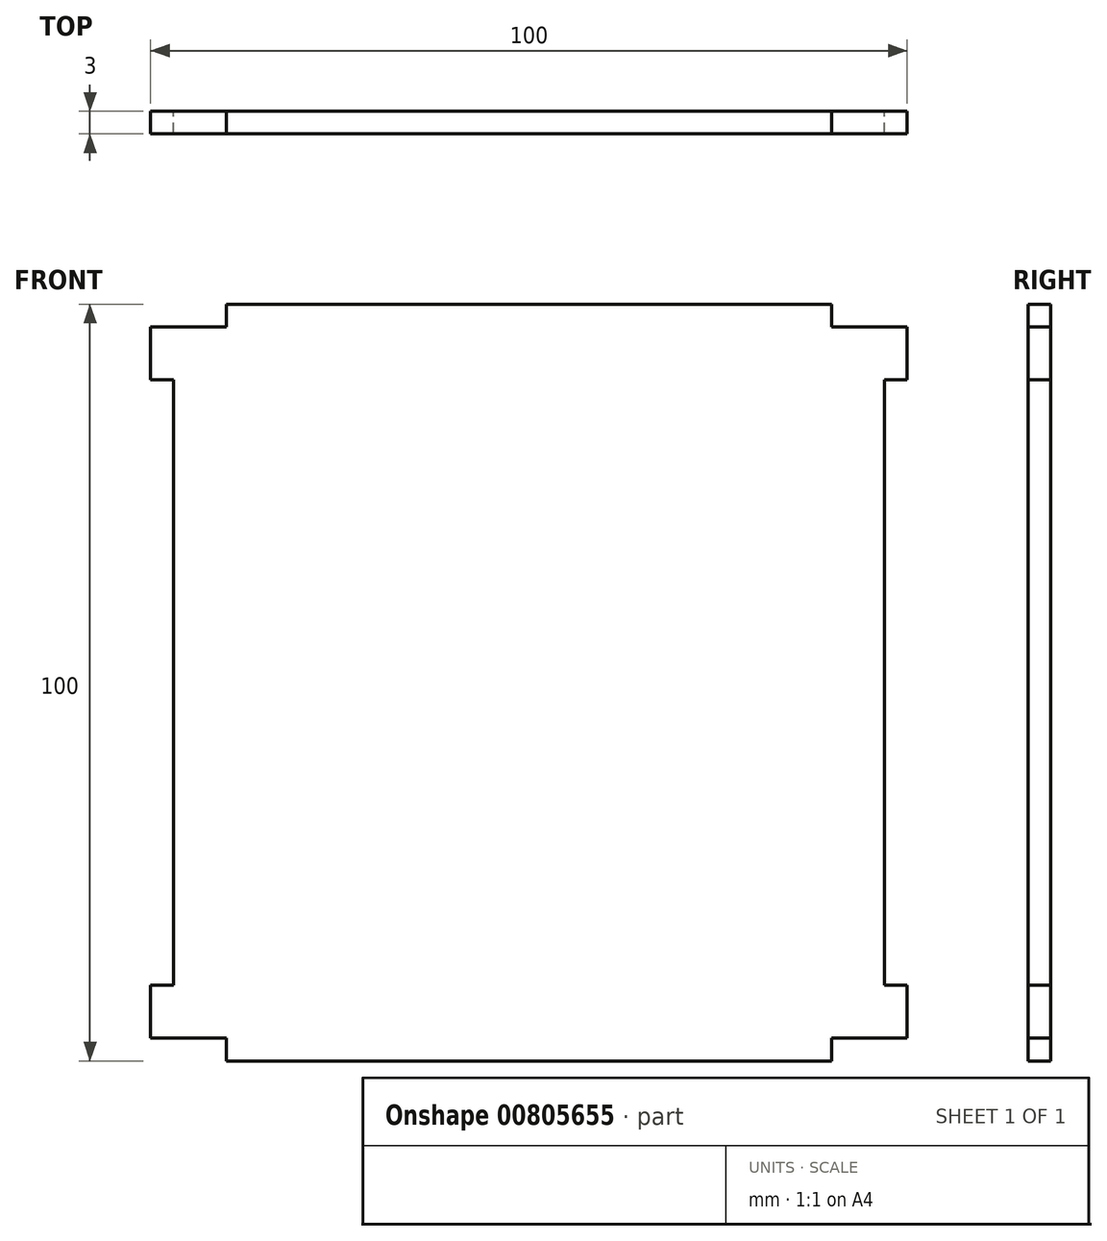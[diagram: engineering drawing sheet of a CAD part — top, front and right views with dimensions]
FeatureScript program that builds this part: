
annotation { "Feature Type Name" : "Feature", "Feature Type Description" : "" }
export const myFeature = defineFeature(function(context is Context, id is Id, definition is map)
    precondition{}
    {
        {
            var Q0;
            Q0=qCreatedBy(makeId("Front.planeOp"),FACE);
            var sketch = newSketch(context, id + "F0", { "sketchPlane" : qUnion([Q0])});
            skLineSegment(sketch, "E0.bottom", {"start": v(10, 0) * mm, "end": v(90, 0) * mm});
            skLineSegment(sketch, "E0.top", {"start": v(10, 100) * mm, "end": v(90, 100) * mm});
            skLineSegment(sketch, "E0.left", {"start": v(0, 3) * mm, "end": v(0, 10) * mm});
            skLineSegment(sketch, "E0.right", {"start": v(100, 3) * mm, "end": v(100, 10) * mm});
            skLineSegment(sketch, "E1", {"start": v(10, 100) * mm, "end": v(10, 97) * mm});
            skLineSegment(sketch, "E2", {"start": v(10, 97) * mm, "end": v(0, 97) * mm});
            skLineSegment(sketch, "E3", {"start": v(50, 100) * mm, "end": v(50, 0) * mm, "construction": true});
            skLineSegment(sketch, "E4", {"start": v(3, 50) * mm, "end": v(97, 50) * mm, "construction": true});
            skPoint(sketch, "E5.orphan", {"position": v(0, 100) * mm});
            skLineSegment(sketch, "E6.MirrorCS", {"start": v(90, 97) * mm, "end": v(100, 97) * mm});
            skLineSegment(sketch, "E7.MirrorCS", {"start": v(90, 100) * mm, "end": v(90, 97) * mm});
            skPoint(sketch, "E8.orphan", {"position": v(100, 100) * mm});
            skLineSegment(sketch, "E9.MirrorCS", {"start": v(10, 3) * mm, "end": v(0, 3) * mm});
            skLineSegment(sketch, "E10.MirrorCS", {"start": v(10, 0) * mm, "end": v(10, 3) * mm});
            skLineSegment(sketch, "E11.MirrorCS", {"start": v(90, 0) * mm, "end": v(90, 3) * mm});
            skLineSegment(sketch, "E12.MirrorCS", {"start": v(90, 3) * mm, "end": v(100, 3) * mm});
            skPoint(sketch, "E13.orphan", {"position": v(100, 0) * mm});
            skPoint(sketch, "E14.orphan", {"position": v(0, 0) * mm});
            skLineSegment(sketch, "E15", {"start": v(3, 90) * mm, "end": v(3, 10) * mm});
            skLineSegment(sketch, "E16", {"start": v(3, 90) * mm, "end": v(0, 90) * mm});
            skLineSegment(sketch, "E17", {"start": v(3, 10) * mm, "end": v(0, 10) * mm});
            skLineSegment(sketch, "E18.trimOffspring", {"start": v(0, 90) * mm, "end": v(0, 97) * mm});
            skPoint(sketch, "E19.orphan", {"position": v(0, 50) * mm});
            skLineSegment(sketch, "E20.MirrorCS", {"start": v(97, 90) * mm, "end": v(100, 90) * mm});
            skLineSegment(sketch, "E21.MirrorCS", {"start": v(97, 90) * mm, "end": v(97, 10) * mm});
            skLineSegment(sketch, "E22.MirrorCS", {"start": v(97, 10) * mm, "end": v(100, 10) * mm});
            skLineSegment(sketch, "E23.trimOffspring", {"start": v(100, 90) * mm, "end": v(100, 97) * mm});
            skPoint(sketch, "E24.orphan", {"position": v(100, 50) * mm});
            skSolve(sketch);
        }
        {
            var Q0;
            Q0=makeQuery(id+"F0.imprint","IMPRINT",FACE,{"disambiguationData":[TD([[makeQuery(id+"F0.imprint","IMPRINT",EDGE,{"derivedFrom":sQuery(id+"F0.wireOp",EDGE,"E0.bottom")}),1.0]])]});
            extrude(context, id + "F1", {"entities" : qUnion([Q0]), "depth" : 3 * mm, "offsetDistance" : 25 * mm});
        }
    });
